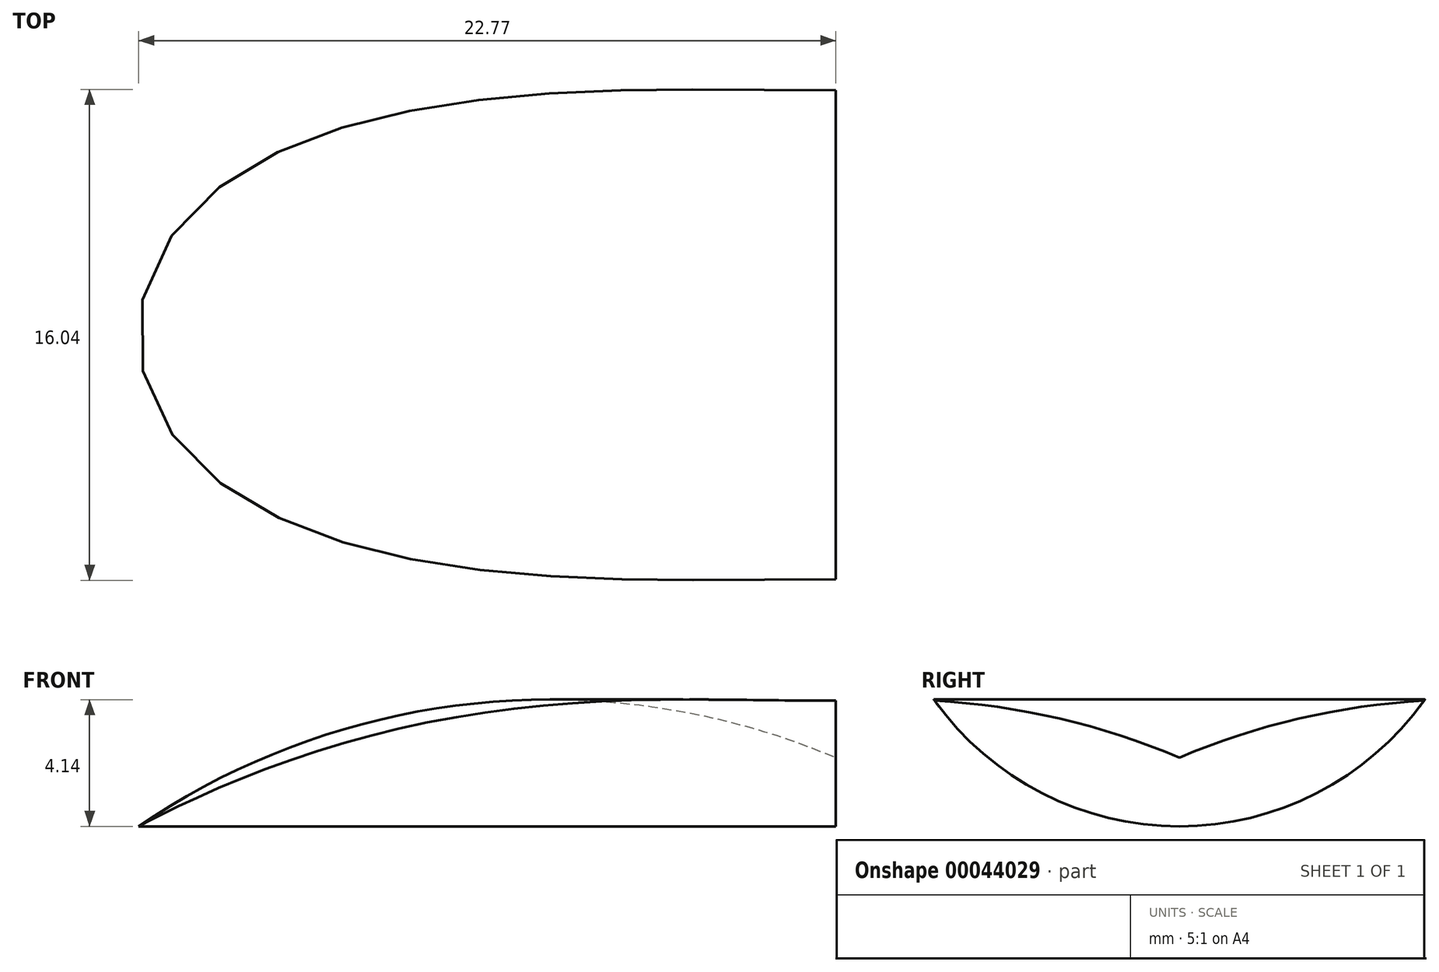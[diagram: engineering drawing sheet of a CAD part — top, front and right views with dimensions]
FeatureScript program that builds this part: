
annotation { "Feature Type Name" : "Feature", "Feature Type Description" : "" }
export const myFeature = defineFeature(function(context is Context, id is Id, definition is map)
    precondition{}
    {
        {
            var Q0;
            Q0=qCreatedBy(makeId("Front.planeOp"),FACE);
            var sketch = newSketch(context, id + "F0", { "sketchPlane" : qUnion([Q0])});
            skLineSegment(sketch, "E0", {"start": v(0, 43.96) * mm, "end": v(0, 0) * mm});
            skArc(sketch, "E1", {"start": v(0, 43.96) * mm, "mid": v(-33.21, 21.98) * mm, "end": v(0, 0) * mm});
            skSolve(sketch);
        }
        {
            var Q0;
            Q0=makeQuery(id+"F0.imprint","IMPRINT",FACE,{"disambiguationData":[TD([[makeQuery(id+"F0.imprint","IMPRINT",EDGE,{"derivedFrom":sQuery(id+"F0.wireOp",EDGE,"E0")}),-1.0]])]});
            var Q1;
            Q1=sQuery(id+"F0.wireOp",EDGE,"E0");
            revolve(context, id + "F1", {"entities" : qUnion([Q0]), "axis" : qUnion([Q1]), "revolveType" : RevolveType.FULL});
        }
        {
            var Q0;
            Q0=qCreatedBy(makeId("Right.planeOp"),FACE);
            var sketch = newSketch(context, id + "F2", { "sketchPlane" : qUnion([Q0])});
            skCircle(sketch, "E2", {"center": v(0, 51.55) * mm, "radius": 9.83 * mm});
            skSolve(sketch);
        }
        {
            var Q0;
            Q0=makeQuery(id+"F2.imprint","IMPRINT",FACE,{"disambiguationData":[TD([[makeQuery(id+"F2.imprint","IMPRINT",EDGE,{"derivedFrom":sQuery(id+"F2.wireOp",EDGE,"E2")}),1.0]])]});
            extrude(context, id + "F3", {"entities" : qUnion([Q0]), "operationType" : NewBodyOperationType.REMOVE, "endBound" : BoundingType.THROUGH_ALL, "oppositeDirection" : true, "depth" : 56.9 * mm});
        }
    });
